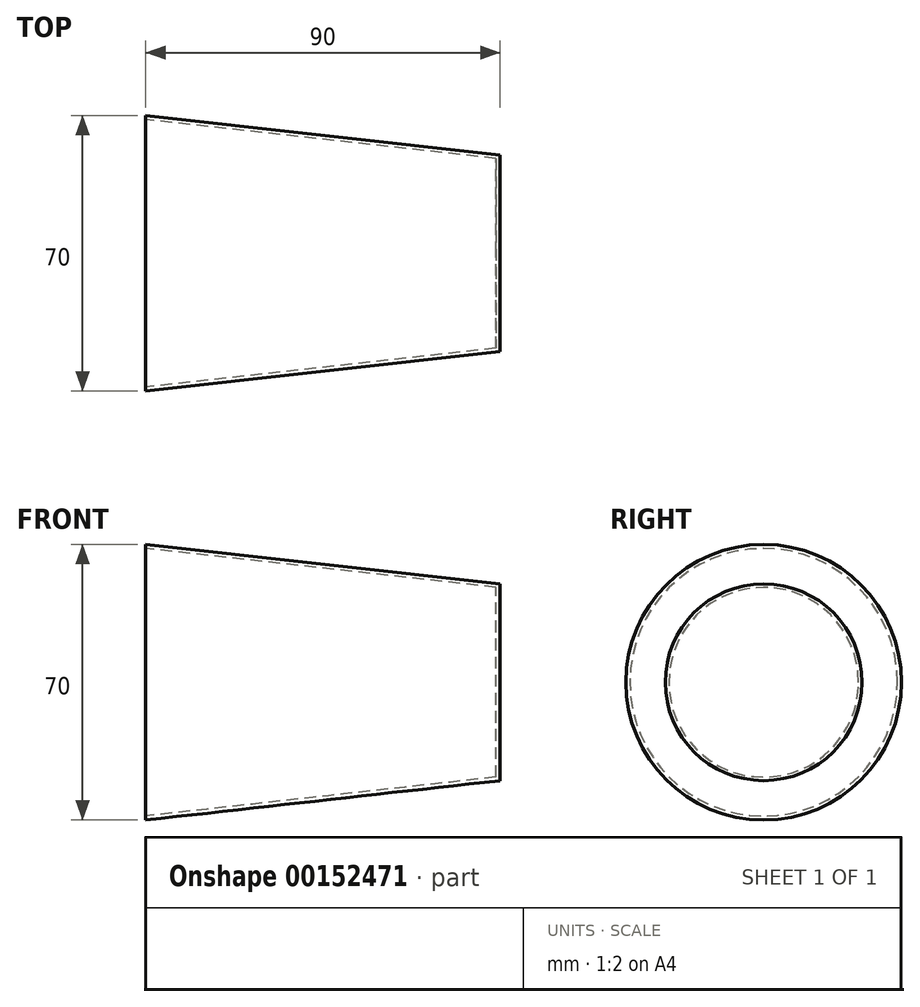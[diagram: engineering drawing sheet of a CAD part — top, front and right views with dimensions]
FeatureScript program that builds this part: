
annotation { "Feature Type Name" : "Feature", "Feature Type Description" : "" }
export const myFeature = defineFeature(function(context is Context, id is Id, definition is map)
    precondition{}
    {
        {
            var Q0;
            Q0=qCreatedBy(makeId("Top.planeOp"),FACE);
            var sketch = newSketch(context, id + "F0", { "sketchPlane" : qUnion([Q0])});
            skLineSegment(sketch, "E0", {"start": v(7.23, -25) * mm, "end": v(-82.77, -35) * mm});
            skLineSegment(sketch, "E1", {"start": v(7.23, -25) * mm, "end": v(7.23, 0) * mm});
            skLineSegment(sketch, "E2", {"start": v(7.23, 0) * mm, "end": v(6.23, 0) * mm});
            skLineSegment(sketch, "E3", {"start": v(6.23, 0) * mm, "end": v(6.23, -24.1) * mm});
            skLineSegment(sketch, "E4", {"start": v(6.23, -24.1) * mm, "end": v(-82.77, -34) * mm});
            skLineSegment(sketch, "E5", {"start": v(-82.77, -34) * mm, "end": v(-82.77, -35) * mm});
            skLineSegment(sketch, "E6", {"start": v(13.6, 0) * mm, "end": v(-107.93, 0) * mm, "construction": true});
            skSolve(sketch);
        }
        {
            var Q0;
            Q0 = qSketchRegion(id + "F0", true);
            var Q1;
            Q1=sQuery(id+"F0.wireOp",EDGE,"E6");
            revolve(context, id + "F1", {"entities" : qUnion([Q0]), "axis" : qUnion([Q1]), "revolveType" : RevolveType.FULL});
        }
    });
